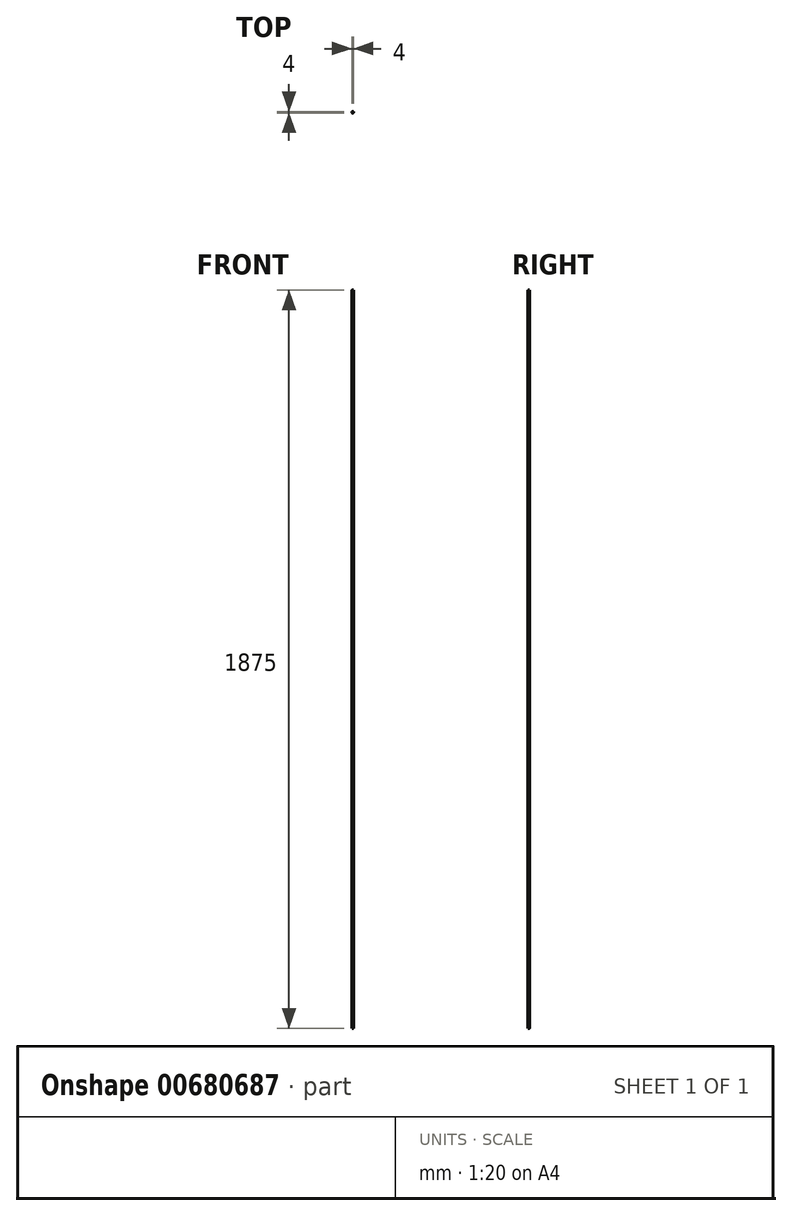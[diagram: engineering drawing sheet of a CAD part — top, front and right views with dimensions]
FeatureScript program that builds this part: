
annotation { "Feature Type Name" : "Feature", "Feature Type Description" : "" }
export const myFeature = defineFeature(function(context is Context, id is Id, definition is map)
    precondition{}
    {
        {
            var Q0;
            Q0=qCreatedBy(makeId("Top.planeOp"),FACE);
            var sketch = newSketch(context, id + "F0", { "sketchPlane" : qUnion([Q0])});
            skCircle(sketch, "E0", {"center": v(0, 0) * mm, "radius": 2 * mm});
            skSolve(sketch);
        }
        {
            var Q0;
            Q0=makeQuery(id+"F0.imprint","IMPRINT",FACE,{"disambiguationData":[TD([[makeQuery(id+"F0.imprint","IMPRINT",EDGE,{"derivedFrom":sQuery(id+"F0.wireOp",EDGE,"E0")}),1.0]])]});
            extrude(context, id + "F1", {"entities" : qUnion([Q0]), "depth" : 1875 * mm, "offsetDistance" : 25 * mm});
        }
    });
